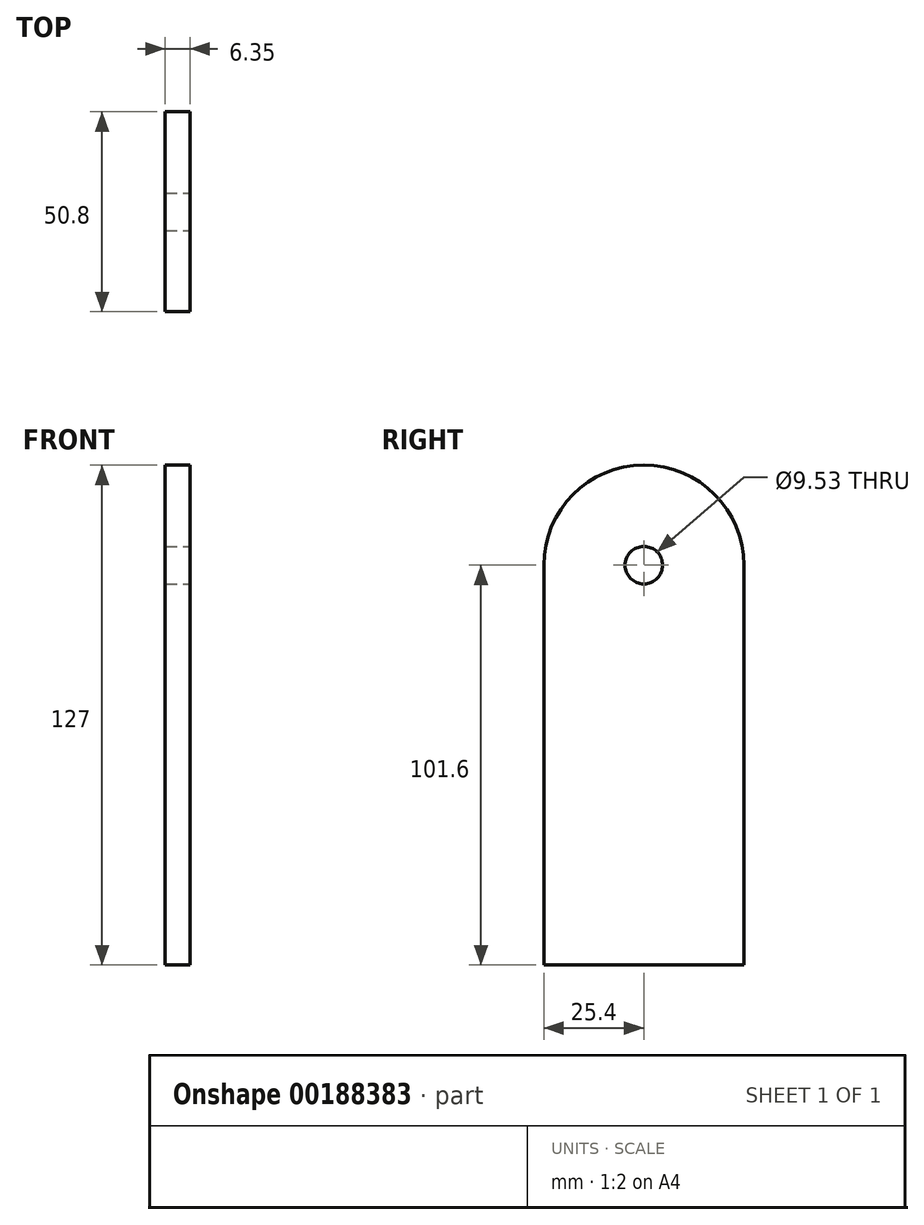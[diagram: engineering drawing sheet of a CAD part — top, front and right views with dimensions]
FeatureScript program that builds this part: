
annotation { "Feature Type Name" : "Feature", "Feature Type Description" : "" }
export const myFeature = defineFeature(function(context is Context, id is Id, definition is map)
    precondition{}
    {
        {
            var Q0;
            Q0=qCreatedBy(makeId("Right.planeOp"),FACE);
            var sketch = newSketch(context, id + "F0", { "sketchPlane" : qUnion([Q0])});
            skLineSegment(sketch, "E0", {"start": v(-25.4, 0) * mm, "end": v(-25.4, -101.6) * mm});
            skLineSegment(sketch, "E1", {"start": v(-25.4, -101.6) * mm, "end": v(25.4, -101.6) * mm});
            skLineSegment(sketch, "E2", {"start": v(25.4, -101.6) * mm, "end": v(25.4, 0) * mm});
            skLineSegment(sketch, "E3", {"start": v(25.4, 0) * mm, "end": v(-25.4, 0) * mm});
            skArc(sketch, "E4", {"start": v(25.4, 0) * mm, "mid": v(0, 25.4) * mm, "end": v(-25.4, 0) * mm});
            skPoint(sketch, "E5", {"position": v(0, 25.4) * mm});
            skSolve(sketch);
        }
        {
            var Q0;
            Q0=makeQuery(id+"F0.imprint","IMPRINT",FACE,{"disambiguationData":[TD([[makeQuery(id+"F0.imprint","IMPRINT",EDGE,{"derivedFrom":sQuery(id+"F0.wireOp",EDGE,"E0")}),1.0]])]});
            var Q1;
            Q1=makeQuery(id+"F0.imprint","IMPRINT",FACE,{"disambiguationData":[TD([[makeQuery(id+"F0.imprint","IMPRINT",EDGE,{"derivedFrom":sQuery(id+"F0.wireOp",EDGE,"E3")}),-1.0]])]});
            extrude(context, id + "F1", {"entities" : qUnion([Q0, Q1]), "depth" : 6.35 * mm});
        }
        {
            var Q0;
            Q0=makeQuery(id+"F1.opExtrude","CAP_FACE",FACE,{"disambiguationData":[OSD([sQuery(id+"F0.wireOp",EDGE,"E0"),sQuery(id+"F0.wireOp",EDGE,"E1"),sQuery(id+"F0.wireOp",EDGE,"E2"),sQuery(id+"F0.wireOp",EDGE,"E4")])],"isStart":false});
            var sketch = newSketch(context, id + "F2", { "sketchPlane" : qUnion([Q0])});
            skCircle(sketch, "E6", {"center": v(0, 0) * mm, "radius": 4.76 * mm});
            skSolve(sketch);
        }
        {
            var Q0;
            Q0=makeQuery(id+"F2.imprint","IMPRINT",FACE,{"disambiguationData":[TD([[makeQuery(id+"F2.imprint","IMPRINT",EDGE,{"derivedFrom":sQuery(id+"F2.wireOp",EDGE,"E6")}),1.0]])]});
            extrude(context, id + "F3", {"entities" : qUnion([Q0]), "operationType" : NewBodyOperationType.REMOVE, "endBound" : BoundingType.UP_TO_NEXT, "oppositeDirection" : true, "depth" : 25.4 * mm});
        }
    });
